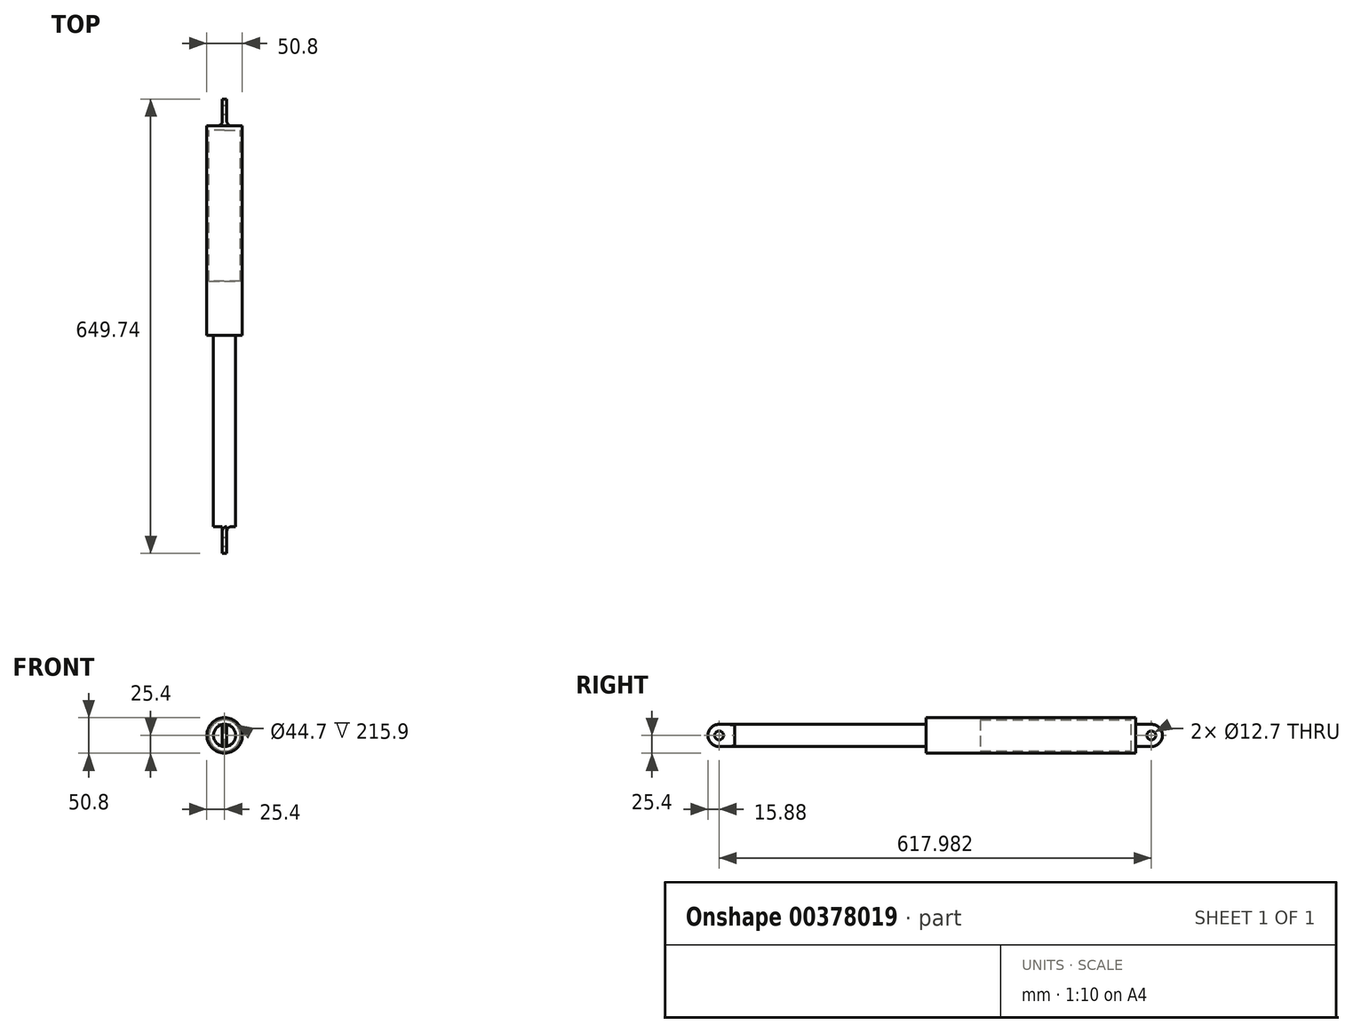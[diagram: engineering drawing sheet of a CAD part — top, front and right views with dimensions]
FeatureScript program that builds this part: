
annotation { "Feature Type Name" : "Feature", "Feature Type Description" : "" }
export const myFeature = defineFeature(function(context is Context, id is Id, definition is map)
    precondition{}
    {
        {
            var Q0;
            Q0=qCreatedBy(makeId("Right.planeOp"),FACE);
            var sketch = newSketch(context, id + "F0", { "sketchPlane" : qUnion([Q0])});
            skArc(sketch, "E0", {"start": v(0, 15.88) * mm, "mid": v(-15.88, 0) * mm, "end": v(0, -15.88) * mm});
            skLineSegment(sketch, "E1", {"start": v(0, 15.88) * mm, "end": v(22.22, 15.88) * mm});
            skLineSegment(sketch, "E2", {"start": v(22.22, 15.88) * mm, "end": v(22.23, -15.88) * mm});
            skCircle(sketch, "E3", {"center": v(0, 0) * mm, "radius": 6.35 * mm});
            skLineSegment(sketch, "E4", {"start": v(0, -15.88) * mm, "end": v(22.23, -15.88) * mm});
            skSolve(sketch);
        }
        {
            var Q0;
            Q0=qSketchRegion(id+"F0",true);
            extrude(context, id + "F1", {"entities" : qUnion([Q0]), "endBound" : BoundingType.SYMMETRIC, "depth" : 6.35 * mm});
        }
        {
            var Q0;
            Q0=makeQuery(id+"F1.opExtrude","SWEPT_FACE",FACE,{"disambiguationData":[OSD([sQuery(id+"F0.wireOp",EDGE,"E2")])]});
            var sketch = newSketch(context, id + "F2", { "sketchPlane" : qUnion([Q0])});
            skCircle(sketch, "E5", {"center": v(0, 0) * mm, "radius": 15.88 * mm});
            skSolve(sketch);
        }
        {
            var Q0;
            Q0=qSketchRegion(id+"F2",true);
            extrude(context, id + "F3", {"entities" : qUnion([Q0]), "operationType" : NewBodyOperationType.ADD, "depth" : 351.28 * mm});
        }
        {
            var Q0;
            {var subQ0=sQuery(id+"F0.wireOp",EDGE,"E2");Q0=makeQuery(id+"F3.boolean.opBoolean","SPLIT",EDGE,{"disambiguationData":[topologyDisambiguationEdgeConnected([makeQuery(id+"F1.opExtrude","CAP_FACE",FACE,{"disambiguationData":[OSD([sQuery(id+"F0.wireOp",EDGE,"E0"),sQuery(id+"F0.wireOp",EDGE,"E1"),subQ0,sQuery(id+"F0.wireOp",EDGE,"E3"),sQuery(id+"F0.wireOp",EDGE,"E4")])],"isStart":false}),makeQuery(id+"F3.opExtrude","CAP_FACE",FACE,{"disambiguationData":[OSD([sQuery(id+"F2.wireOp",EDGE,"E5")])],"isStart":true})])],"derivedFrom":makeQuery(id+"F1.opExtrude","CAP_EDGE",EDGE,{"disambiguationData":[OSD([subQ0])],"isStart":false})});}
            var Q1;
            {var subQ0=sQuery(id+"F0.wireOp",EDGE,"E2");Q1=makeQuery(id+"F3.boolean.opBoolean","SPLIT",EDGE,{"disambiguationData":[topologyDisambiguationEdgeConnected([makeQuery(id+"F1.opExtrude","CAP_FACE",FACE,{"disambiguationData":[OSD([sQuery(id+"F0.wireOp",EDGE,"E0"),sQuery(id+"F0.wireOp",EDGE,"E1"),subQ0,sQuery(id+"F0.wireOp",EDGE,"E3"),sQuery(id+"F0.wireOp",EDGE,"E4")])],"isStart":true}),makeQuery(id+"F3.opExtrude","CAP_FACE",FACE,{"disambiguationData":[OSD([sQuery(id+"F2.wireOp",EDGE,"E5")])],"isStart":true})])],"derivedFrom":makeQuery(id+"F1.opExtrude","CAP_EDGE",EDGE,{"disambiguationData":[OSD([subQ0])],"isStart":true})});}
            fillet(context, id + "F4", {"entities" : qUnion([Q0, Q1]), "radius" : 6.35 * mm, "tangentPropagation" : true, "allowEdgeOverflow" : false});
        }
        {
            var Q0;
            Q0=qCreatedBy(makeId("Right.planeOp"),FACE);
            var sketch = newSketch(context, id + "F5", { "sketchPlane" : qUnion([Q0])});
            skCircle(sketch, "E6", {"center": v(617.98, 0) * mm, "radius": 6.35 * mm});
            skArc(sketch, "E7", {"start": v(617.98, -15.87) * mm, "mid": v(633.86, 0) * mm, "end": v(617.98, 15.88) * mm});
            skLineSegment(sketch, "E8", {"start": v(617.98, 15.88) * mm, "end": v(595.76, 15.88) * mm});
            skLineSegment(sketch, "E9", {"start": v(595.76, 15.88) * mm, "end": v(595.76, -15.88) * mm});
            skLineSegment(sketch, "E10", {"start": v(617.98, -15.87) * mm, "end": v(595.76, -15.88) * mm});
            skSolve(sketch);
        }
        {
            var Q0;
            Q0=qSketchRegion(id+"F5",true);
            extrude(context, id + "F6", {"entities" : qUnion([Q0]), "endBound" : BoundingType.SYMMETRIC, "depth" : 6.35 * mm});
        }
        {
            var Q0;
            Q0=makeQuery(id+"F6.opExtrude","SWEPT_FACE",FACE,{"disambiguationData":[OSD([sQuery(id+"F5.wireOp",EDGE,"E9")])]});
            var sketch = newSketch(context, id + "F7", { "sketchPlane" : qUnion([Q0])});
            skCircle(sketch, "E11", {"center": v(0, 0) * mm, "radius": 25.4 * mm});
            skCircle(sketch, "E12.0.0", {"center": v(0, 0) * mm, "radius": 15.88 * mm, "construction": true});
            skCircle(sketch, "E13", {"center": v(0, 0) * mm, "radius": 22.35 * mm});
            skSolve(sketch);
        }
        {
            var Q0;
            Q0=qSketchRegion(id+"F7",true);
            extrude(context, id + "F8", {"entities" : qUnion([Q0]), "depth" : 300 * mm});
        }
        {
            var Q0;
            Q0=makeQuery(id+"F6.opExtrude","SWEPT_FACE",FACE,{"disambiguationData":[OSD([sQuery(id+"F5.wireOp",EDGE,"E9")])]});
            var sketch = newSketch(context, id + "F9", { "sketchPlane" : qUnion([Q0])});
            skCircle(sketch, "E14.0", {"center": v(0, 0) * mm, "radius": 22.35 * mm});
            skSolve(sketch);
        }
        {
            var Q0;
            Q0=qSketchRegion(id+"F9",true);
            extrude(context, id + "F10", {"entities" : qUnion([Q0]), "operationType" : NewBodyOperationType.ADD, "depth" : 6.35 * mm});
        }
        {
            var Q0;
            {var subQ0=sQuery(id+"F5.wireOp",EDGE,"E9");Q0=makeQuery(id+"F10.boolean.opBoolean","SPLIT",EDGE,{"disambiguationData":[topologyDisambiguationEdgeConnected([makeQuery(id+"F6.opExtrude","CAP_FACE",FACE,{"disambiguationData":[OSD([sQuery(id+"F5.wireOp",EDGE,"E6"),sQuery(id+"F5.wireOp",EDGE,"E7"),sQuery(id+"F5.wireOp",EDGE,"E8"),subQ0,sQuery(id+"F5.wireOp",EDGE,"E10")])],"isStart":true}),makeQuery(id+"F10.opExtrude","CAP_FACE",FACE,{"disambiguationData":[OSD([sQuery(id+"F9.wireOp",EDGE,"0a1f69fb-0a38-4f9e-a69e-4767d570a797.0")])],"isStart":true})])],"derivedFrom":makeQuery(id+"F6.opExtrude","CAP_EDGE",EDGE,{"disambiguationData":[OSD([subQ0])],"isStart":true})});}
            var Q1;
            {var subQ0=sQuery(id+"F5.wireOp",EDGE,"E9");Q1=makeQuery(id+"F10.boolean.opBoolean","SPLIT",EDGE,{"disambiguationData":[topologyDisambiguationEdgeConnected([makeQuery(id+"F6.opExtrude","CAP_FACE",FACE,{"disambiguationData":[OSD([sQuery(id+"F5.wireOp",EDGE,"E6"),sQuery(id+"F5.wireOp",EDGE,"E7"),sQuery(id+"F5.wireOp",EDGE,"E8"),subQ0,sQuery(id+"F5.wireOp",EDGE,"E10")])],"isStart":false}),makeQuery(id+"F10.opExtrude","CAP_FACE",FACE,{"disambiguationData":[OSD([sQuery(id+"F9.wireOp",EDGE,"0a1f69fb-0a38-4f9e-a69e-4767d570a797.0")])],"isStart":true})])],"derivedFrom":makeQuery(id+"F6.opExtrude","CAP_EDGE",EDGE,{"disambiguationData":[OSD([subQ0])],"isStart":false})});}
            fillet(context, id + "F11", {"entities" : qUnion([Q0, Q1]), "radius" : 6.35 * mm, "tangentPropagation" : true, "allowEdgeOverflow" : false});
        }
        {
            var Q0;
            Q0=makeQuery(id+"F8.opExtrude","CAP_FACE",FACE,{"disambiguationData":[OSD([sQuery(id+"F7.wireOp",EDGE,"E11"),sQuery(id+"F7.wireOp",EDGE,"E13")])],"isStart":false});
            var sketch = newSketch(context, id + "F12", { "sketchPlane" : qUnion([Q0])});
            skCircle(sketch, "E15.0", {"center": v(0, 0) * mm, "radius": 22.35 * mm});
            skCircle(sketch, "E16.0", {"center": v(0, 0) * mm, "radius": 15.88 * mm});
            skSolve(sketch);
        }
        {
            var Q0;
            Q0=qSketchRegion(id+"F12",true);
            extrude(context, id + "F13", {"entities" : qUnion([Q0]), "operationType" : NewBodyOperationType.ADD, "oppositeDirection" : true, "depth" : 6.35 * mm});
        }
        {
            var Q0;
            Q0=makeQuery(id+"F3.opExtrude","CAP_FACE",FACE,{"disambiguationData":[OSD([sQuery(id+"F2.wireOp",EDGE,"E5")])],"isStart":false});
            var sketch = newSketch(context, id + "F14", { "sketchPlane" : qUnion([Q0])});
            skCircle(sketch, "E17.0", {"center": v(0, 0) * mm, "radius": 25.4 * mm, "construction": true});
            skCircle(sketch, "E18", {"center": v(0, 0) * mm, "radius": 22.35 * mm});
            skCircle(sketch, "E19.0", {"center": v(0, 0) * mm, "radius": 15.88 * mm});
            skSolve(sketch);
        }
        {
            var Q0;
            Q0=qSketchRegion(id+"F14",true);
            extrude(context, id + "F15", {"entities" : qUnion([Q0]), "operationType" : NewBodyOperationType.ADD, "endBound" : BoundingType.UP_TO_NEXT, "oppositeDirection" : true, "depth" : 25 * mm});
        }
    });
